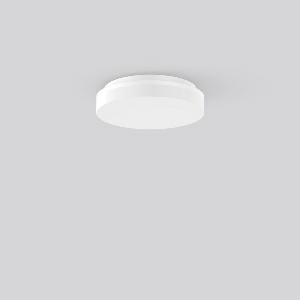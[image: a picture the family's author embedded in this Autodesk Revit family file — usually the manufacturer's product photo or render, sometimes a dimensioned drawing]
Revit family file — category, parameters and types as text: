
# Revit family: hb_505_221186_002_2_0459
name_source: partatom
category: Lighting Fixtures
units: mm (PartAtom-declared; Revit-internal decimal feet)

## family parameters
Cut with Voids When Loaded = No
Host = Face
Light Source = No
Part Type = Normal
Room Calculation Point = No
Round Connector Dimension = Use Diameter
Shared = No

## types (1)
- MultiColor 830 (1 x LED Modul 830, 1350 lm, 3000)
    Apparent Load = 15 VA
    CIE Flux Codes = 43 74 92 90 100
    Color Rendering = 80
    Color Temperature = 3000
    Default Elevation = 1800 mm
    Description = Series: HB 505
Ceiling and wall luminaire with slim design. Housing: plastic (polycarbonate). Diffuser: plastic (polycarbonate), opal. Base and diffuser are sealed together. MultiColour: Colour temperature adjustable via switching element. Choice of 3000 K or 4000 K. Factory setting is 3000 K. Quick mounting adapter galvanized steel sheet, with fastening screws. Driver integrated. 
Colour: white
Diameter: 220 mm
Height: 53 mm
Lamp: LED
Socket: without socket
Colour temperature: 3000K, 4000K
Colour rendering index (CRI): 80
System power: 15 W
Rated luminous flux: 1350 lm
Luminous efficiency: 90 lm/W
System power 2: 15 W
Rated luminous flux 2: 1400 lm
Luminous efficiency 2: 93 lm/W
Control gear: EB
Protection class: I
Type of protection: IP 20
    Height = 53 mm
    Lamp = 1 x LED Modul 830
    Lamp Light Flux = 1350 lm
    Lamp count = 1
    Length = 220 mm
    Lifetime = 50000 h
    Luminous efficacy = 90 lm/W
    Manufacturer = RZB
    ModVariant = No
    Model = 221186.002.2
    Mounting Place = Ceiling, Wall
    Mounting Type = Surface mounted
    Number of Poles = 1
    OnlyDefault = Yes
    Power Factor = 1
    Product Name = HB 505
    Product group = Surface mounted ceiling and wall luminaires
    ProductGroupID = 305
    Protection Class = Protection class I
    Protection Degree = IP 20
    RLX_Detail_Level = 1
    RLX_Emergency_Light_Flux = 0 lm
    RLX_Emergency_Type = 0
    RLX_Emergency_Type_DB = No
    RlxData = <blob elided: 25305 chars, md5=34e6c5a2>
    Socket = socket
    Standby Power = 0 W
    System Light Flux = 1350 lm
    System Power = 15 W
    Type Comments = MultiColor 830
    Type Image = 221186.002.jpg
    URL = http://relux.com
    VarID = multicolor_830
    Voltage = 230 V
    Voltage Range = 220-240 V
    Weight = 0.00 kg
    Width = 0 mm  [stored 0 ft]

note: [stored X ft] marks values corroborated as IEEE doubles in the binary element streams (Revit-internal decimal feet)

## geometry (parser evidence)
native form markers: Blend x4, Sweep x14
no freeform markers — native parametric forms only
